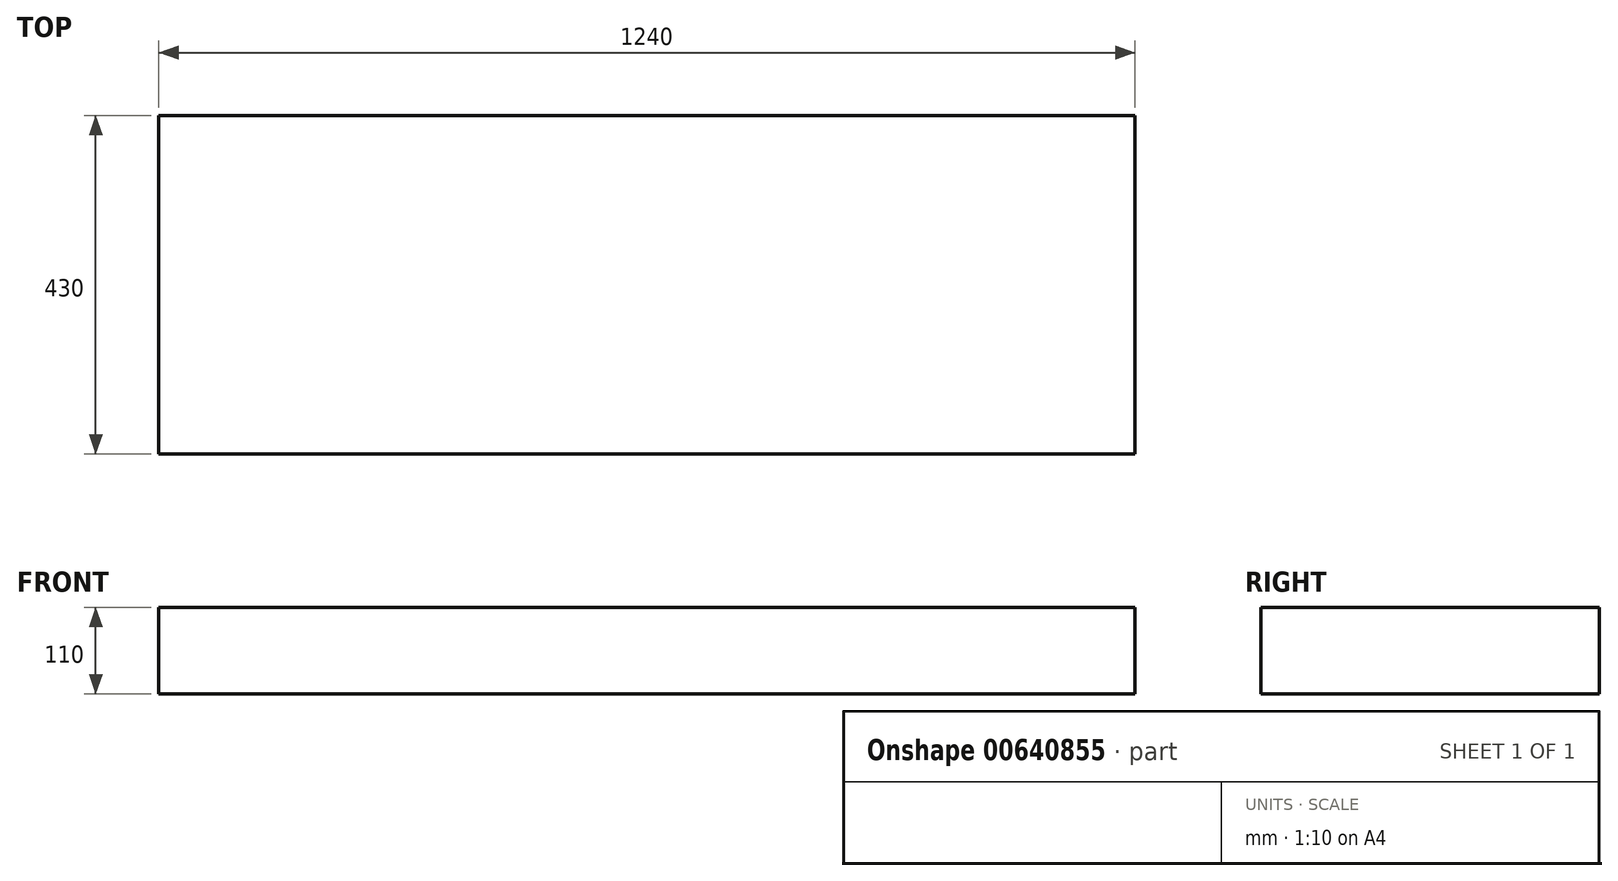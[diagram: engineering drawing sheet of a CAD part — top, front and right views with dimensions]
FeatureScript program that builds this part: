
annotation { "Feature Type Name" : "Feature", "Feature Type Description" : "" }
export const myFeature = defineFeature(function(context is Context, id is Id, definition is map)
    precondition{}
    {
        {
            var Q0;
            Q0=qCreatedBy(makeId("Top.planeOp"),FACE);
            var sketch = newSketch(context, id + "F0", { "sketchPlane" : qUnion([Q0])});
            skLineSegment(sketch, "E0.bottom", {"start": v(620, 239.29) * mm, "end": v(-620, 239.29) * mm});
            skLineSegment(sketch, "E0.top", {"start": v(620, -190.71) * mm, "end": v(-620, -190.71) * mm});
            skLineSegment(sketch, "E0.left", {"start": v(620, 239.29) * mm, "end": v(620, -190.71) * mm});
            skLineSegment(sketch, "E0.right", {"start": v(-620, 239.29) * mm, "end": v(-620, -190.71) * mm});
            skPoint(sketch, "E0.middle", {"position": v(0, 24.29) * mm});
            skSolve(sketch);
        }
        {
            var Q0;
            Q0=makeQuery(id+"F0.imprint","IMPRINT",FACE,{"disambiguationData":[TD([[makeQuery(id+"F0.imprint","IMPRINT",EDGE,{"derivedFrom":sQuery(id+"F0.wireOp",EDGE,"E0.bottom")}),1.0]])]});
            extrude(context, id + "F1", {"entities" : qUnion([Q0]), "depth" : 110 * mm, "offsetDistance" : 25 * mm});
        }
    });
